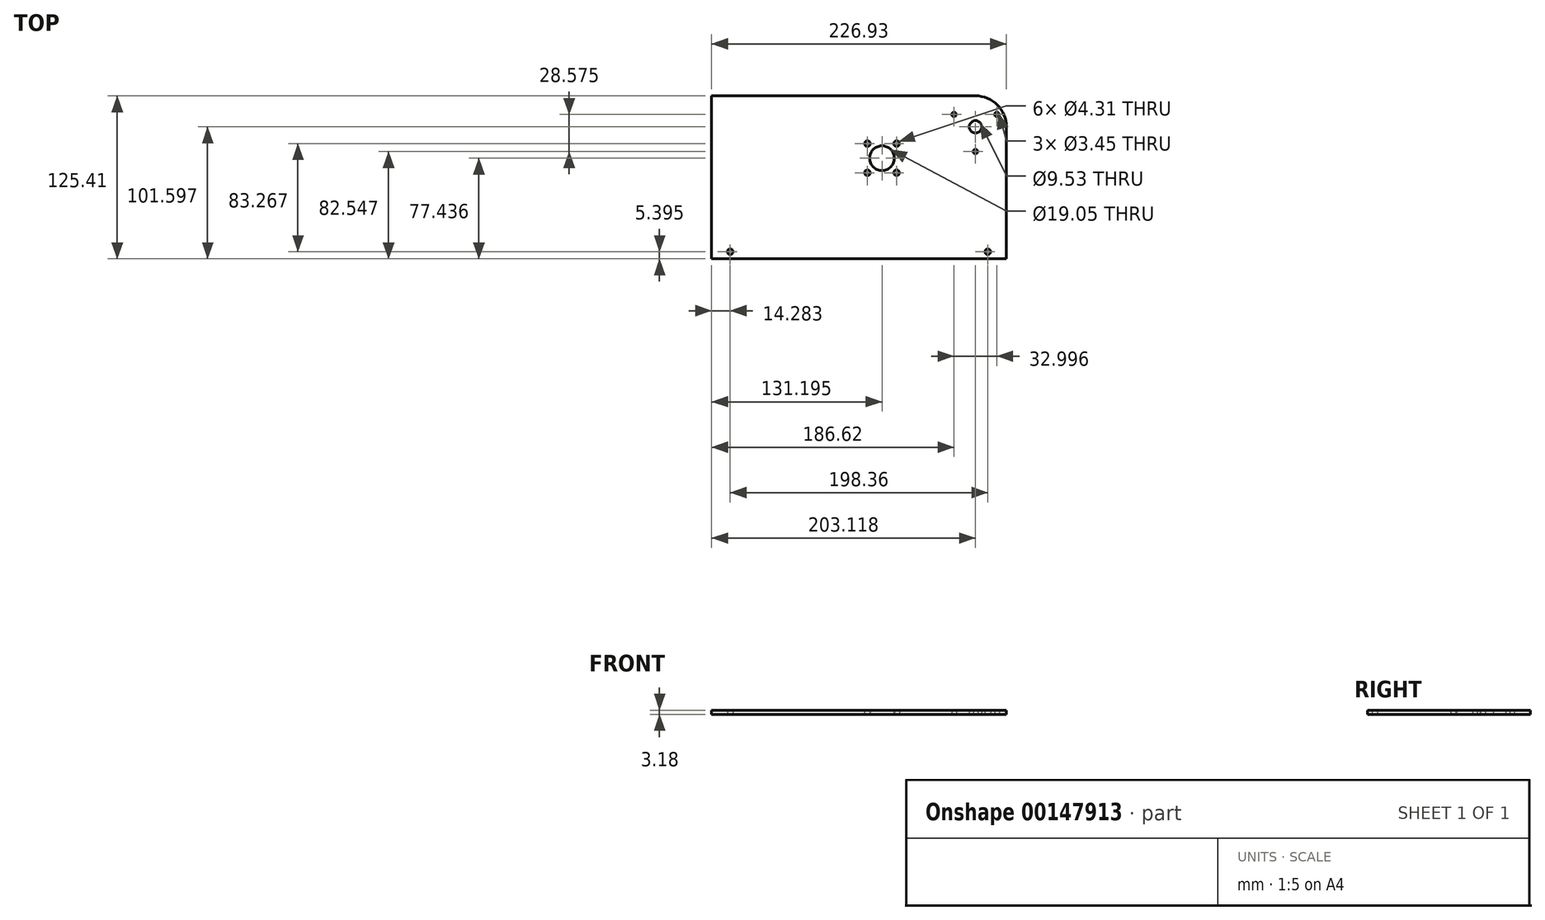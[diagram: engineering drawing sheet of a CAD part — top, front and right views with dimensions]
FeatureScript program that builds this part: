
annotation { "Feature Type Name" : "Feature", "Feature Type Description" : "" }
export const myFeature = defineFeature(function(context is Context, id is Id, definition is map)
    precondition{}
    {
        {
            var Q0;
            Q0=qCreatedBy(makeId("Top.planeOp"),FACE);
            var sketch = newSketch(context, id + "F0", { "sketchPlane" : qUnion([Q0])});
            skCircle(sketch, "E0", {"center": v(-23.81, -23.81) * mm, "radius": 4.76 * mm});
            skCircle(sketch, "E1.cCircle", {"center": v(-23.81, -23.81) * mm, "radius": 9.52 * mm, "construction": true});
            skLineSegment(sketch, "E1.0", {"start": v(-40.31, -14.29) * mm, "end": v(-7.31, -14.29) * mm, "construction": true});
            skLineSegment(sketch, "E1.1", {"start": v(-7.31, -14.29) * mm, "end": v(-23.81, -42.86) * mm, "construction": true});
            skLineSegment(sketch, "E1.2", {"start": v(-23.81, -42.86) * mm, "end": v(-40.31, -14.29) * mm, "construction": true});
            skPoint(sketch, "E1.0.midPoint", {"position": v(-23.81, -14.29) * mm});
            skCircle(sketch, "E2", {"center": v(-23.81, -23.81) * mm, "radius": 14.29 * mm, "construction": true});
            skCircle(sketch, "E3", {"center": v(-40.31, -14.29) * mm, "radius": 4.76 * mm, "construction": true});
            skCircle(sketch, "E4", {"center": v(-40.31, -14.29) * mm, "radius": 1.73 * mm});
            skCircle(sketch, "E5", {"center": v(-7.31, -14.29) * mm, "radius": 1.73 * mm});
            skCircle(sketch, "E6", {"center": v(-23.81, -42.86) * mm, "radius": 1.73 * mm});
            skLineSegment(sketch, "E7.bottom", {"start": v(-226.93, 0) * mm, "end": v(0, 0) * mm});
            skLineSegment(sketch, "E7.top", {"start": v(-226.93, -125.41) * mm, "end": v(0, -125.41) * mm});
            skLineSegment(sketch, "E7.left", {"start": v(-226.93, 0) * mm, "end": v(-226.93, -125.41) * mm});
            skLineSegment(sketch, "E7.right", {"start": v(0, 0) * mm, "end": v(0, -125.41) * mm});
            skCircle(sketch, "E8", {"center": v(-23.81, -23.81) * mm, "radius": 23.81 * mm, "construction": true});
            skLineSegment(sketch, "E9", {"start": v(0, -120.02) * mm, "end": v(-14.29, -120.02) * mm, "construction": true});
            skLineSegment(sketch, "E10", {"start": v(-226.93, -120.02) * mm, "end": v(-212.65, -120.02) * mm, "construction": true});
            skLineSegment(sketch, "E11", {"start": v(-14.29, -120.02) * mm, "end": v(-14.29, -125.41) * mm, "construction": true});
            skCircle(sketch, "E12", {"center": v(-14.29, -120.02) * mm, "radius": 2.15 * mm});
            skCircle(sketch, "E13", {"center": v(-212.65, -120.02) * mm, "radius": 2.15 * mm});
            skLineSegment(sketch, "E14", {"start": v(-23.81, -23.81) * mm, "end": v(-95.74, -47.97) * mm, "construction": true});
            skCircle(sketch, "E15", {"center": v(-95.74, -47.97) * mm, "radius": 9.53 * mm});
            skLineSegment(sketch, "E16.bottom", {"start": v(-84.51, -59.2) * mm, "end": v(-106.96, -59.2) * mm, "construction": true});
            skLineSegment(sketch, "E16.top", {"start": v(-84.51, -36.75) * mm, "end": v(-106.96, -36.75) * mm, "construction": true});
            skLineSegment(sketch, "E16.left", {"start": v(-84.51, -59.2) * mm, "end": v(-84.51, -36.75) * mm, "construction": true});
            skLineSegment(sketch, "E16.right", {"start": v(-106.96, -59.2) * mm, "end": v(-106.96, -36.75) * mm, "construction": true});
            skCircle(sketch, "E17", {"center": v(-95.74, -47.97) * mm, "radius": 11.11 * mm, "construction": true});
            skCircle(sketch, "E18", {"center": v(-84.51, -36.75) * mm, "radius": 4.76 * mm, "construction": true});
            skCircle(sketch, "E19", {"center": v(-106.96, -36.75) * mm, "radius": 2.15 * mm});
            skCircle(sketch, "E20", {"center": v(-84.51, -36.75) * mm, "radius": 2.15 * mm});
            skCircle(sketch, "E21", {"center": v(-84.51, -59.2) * mm, "radius": 2.15 * mm});
            skCircle(sketch, "E22", {"center": v(-106.96, -59.2) * mm, "radius": 2.15 * mm});
            skSolve(sketch);
        }
        {
            var Q0;
            Q0=qSketchRegion(id+"F0",true);
            extrude(context, id + "F1", {"entities" : qUnion([Q0]), "depth" : 3.17 * mm});
        }
        {
            var Q0;
            Q0=makeQuery(id+"F1.opExtrude","SWEPT_EDGE",EDGE,{"disambiguationData":[OSD([sQuery(id+"F0.wireOp",EDGE,"E7.bottom"),sQuery(id+"F0.wireOp",EDGE,"E7.right")])]});
            fillet(context, id + "F2", {"entities" : qUnion([Q0]), "radius" : 23.8 * mm, "tangentPropagation" : true, "allowEdgeOverflow" : false});
        }
    });
